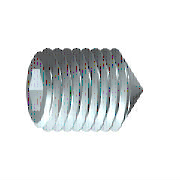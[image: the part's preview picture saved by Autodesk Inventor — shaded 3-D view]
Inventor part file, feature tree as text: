
AUTODESK INVENTOR PART (.ipt)
format: ipt  version: 2023.3 (Build 273359000, 359)  size: 164,864 bytes
history: native  units: mm (DEFAULTED — no unit token found)
features: other x2, sketch x2, extrude x1, plane x1
ambient origin geometry x8: Origin, YZ Plane, XZ Plane, XY Plane, X Axis, Y Axis, Z Axis, Center Point
bodies: Solid1 (feature_tree)
feature tree (6):
  other  "Körper"
  extrude  "Loch"  TaperAngle=60.0deg  [1 undecoded]
  other  "Work Axis1"
  plane  "Work Plane1"
  sketch  "Skizze1"  dims[d0=0.8mm d1=60.0deg]
  sketch  "Skizze2"  dims[d2=2.0mm d3=1.03923mm d6=90.0deg d4=0.0mm d5=3.0mm d21=10.0mm d7=0.0mm d8=0.433013mm d9=60.0deg d10=0.24538mm d11=60.0deg d12=3.0mm d13=0.0mm d34=0.433013mm d35=0.24538mm d36=0.0mm d37=0.0mm]
note: 1 required parameter value undecoded (feature->parameter linkage not recoverable at this tier; creation-order binding heuristic only, values carry confidence <= 0.55)
